# Revit family: TV-012_RFA
name_source: partatom
category: Plumbing Fixtures
units: mm (PartAtom-declared; Revit-internal decimal feet)

## family parameters
Always vertical = Yes
Cut with Voids When Loaded = No
OmniClass Number = 23.45.00.00
OmniClass Title = Sanitary, Laundry, and Cleaning Equipment
Part Type = Normal
Room Calculation Point = No
Round Connector Dimension = Use Diameter
Shared = Yes
Work Plane-Based = Yes

## types (1)
- TV-012
    Características del Producto = Válvula de paso.
    Cuerpo de Latón = Brass
    Default Elevation = 0"
    Description = Válvula de control de apertura y cierre del flujo
de agua.
    Garantía = El producto HELVEX está garantizado como libre de defectos en materiales y procesos de fabricación. El producto HELVEX está garantizado, en lo que se refiere a los acabados; por un periodo de 10 años en los acabados cromo y duravex, y por 2 años en acabados diferentes al cromo, a partir de la fecha de compra indicada en la factura.
    Instalación = Conexión ½ - 14 NPSM
    Manufacturer = HELVEX S.A. de C.V.
    Model = TV-012
    Operación = Gire el maneral en sentido de las manecillas del
reloj para abrir y en sentido contrario para
cerrar.
    Presión Máxima de Trabajo = 85.3 psi
    Presión Mínima de Trabajo = 3.5 psi
    Profundidad Total = 3"
    Type Comments = Válvula de paso.

## geometry (parser evidence)
native form markers: Sweep x3
no freeform markers — native parametric forms only
